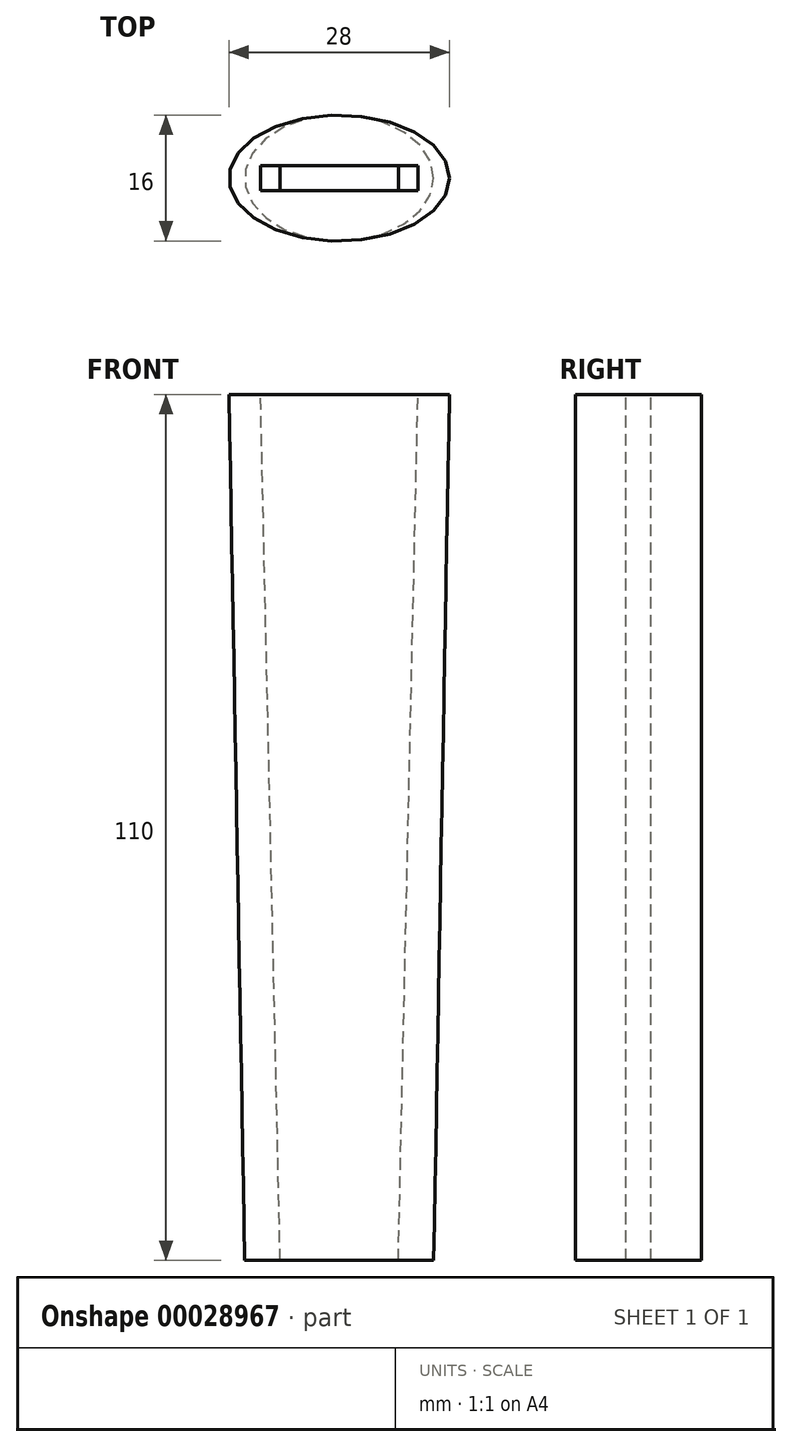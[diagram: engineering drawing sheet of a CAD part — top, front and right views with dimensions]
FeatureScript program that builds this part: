
annotation { "Feature Type Name" : "Feature", "Feature Type Description" : "" }
export const myFeature = defineFeature(function(context is Context, id is Id, definition is map)
    precondition{}
    {
        {
            var Q0;
            Q0=qCreatedBy(makeId("Top.planeOp"),FACE);
            var sketch = newSketch(context, id + "F0", { "sketchPlane" : qUnion([Q0])});
            skPoint(sketch, "E0", {"position": v(0, 0) * mm});
            skPoint(sketch, "E1", {"position": v(0, 8) * mm});
            skPoint(sketch, "E2", {"position": v(12, 0) * mm});
            skLineSegment(sketch, "E3", {"start": v(0, 0) * mm, "end": v(0, 8) * mm, "construction": true});
            skLineSegment(sketch, "E4", {"start": v(0, 0) * mm, "end": v(12, 0) * mm, "construction": true});
            skEllipse(sketch, "E5", {"center": v(0, 0) * mm, "majorRadius": 12 * mm, "minorRadius": 8 * mm, "majorAxis": v(1, 0)});
            skSolve(sketch);
        }
        {
            var Q0;
            Q0=makeQuery(id+"F0.imprint","IMPRINT",FACE,{"disambiguationData":[TD([[makeQuery(id+"F0.imprint","IMPRINT",EDGE,{"derivedFrom":sQuery(id+"F0.wireOp",EDGE,"E5")}),1.0]])]});
            cPlane(context, id + "F1", {"entities" : qUnion([Q0]), "cplaneType" : CPlaneType.OFFSET, "offset" : 110 * mm, "width" : 150 * mm, "height" : 150 * mm});
        }
        {
            var Q0;
            Q0=qCreatedBy(id+"F1.planeOp",FACE);
            var sketch = newSketch(context, id + "F2", { "sketchPlane" : qUnion([Q0])});
            skEllipse(sketch, "E6", {"center": v(0, 0) * mm, "majorRadius": 14 * mm, "minorRadius": 8 * mm, "majorAxis": v(-1, 0)});
            skSolve(sketch);
        }
        {
            var Q0;
            Q0=makeQuery(id+"F0.imprint","IMPRINT",FACE,{"disambiguationData":[TD([[makeQuery(id+"F0.imprint","IMPRINT",EDGE,{"derivedFrom":sQuery(id+"F0.wireOp",EDGE,"E5")}),1.0]])]});
            var Q1;
            Q1=makeQuery(id+"F2.imprint","IMPRINT",FACE,{"disambiguationData":[TD([[makeQuery(id+"F2.imprint","IMPRINT",EDGE,{"derivedFrom":sQuery(id+"F2.wireOp",EDGE,"E6")}),1.0]])]});
            loft(context, id + "F3", {"sheetProfilesArray" : [{ "sheetProfileEntities" : qUnion([Q0]) }, { "sheetProfileEntities" : qUnion([Q1]) }]});
        }
        {
            var Q0;
            Q0=makeQuery(id+"F3.opLoft","CAP_FACE",FACE,{"disambiguationData":[OSD([makeQuery(id+"F0.imprint","IMPRINT",FACE,{"disambiguationData":[TD([[makeQuery(id+"F0.imprint","IMPRINT",EDGE,{"derivedFrom":sQuery(id+"F0.wireOp",EDGE,"E5")}),1.0]])]})])],"isStart":true});
            var sketch = newSketch(context, id + "F4", { "sketchPlane" : qUnion([Q0])});
            skSolve(sketch);
        }
        {
            var Q0;
            Q0=makeQuery(id+"F4.imprint","IMPRINT",FACE,{"disambiguationData":[TD([[makeQuery(id+"F4.imprint","IMPRINT",EDGE,{"derivedFrom":makeQuery(id+"F3.opLoft","MID_CAP_EDGE",EDGE,{"disambiguationData":[OSD([sQuery(id+"F0.wireOp",EDGE,"E5")])],"capPos":0.0})}),1.0]])]});
            var sketch = newSketch(context, id + "F5", { "sketchPlane" : qUnion([Q0])});
            skLineSegment(sketch, "E7.rect.bottom", {"start": v(7.5, 1.6) * mm, "end": v(-7.5, 1.6) * mm});
            skLineSegment(sketch, "E7.rect.top", {"start": v(7.5, -1.6) * mm, "end": v(-7.5, -1.6) * mm});
            skLineSegment(sketch, "E7.rect.left", {"start": v(7.5, 1.6) * mm, "end": v(7.5, -1.6) * mm});
            skLineSegment(sketch, "E7.rect.right", {"start": v(-7.5, 1.6) * mm, "end": v(-7.5, -1.6) * mm});
            skPoint(sketch, "E7.rect.middle", {"position": v(0, 0) * mm});
            skSolve(sketch);
        }
        {
            var Q0;
            Q0=makeQuery(id+"F3.opLoft","CAP_FACE",FACE,{"disambiguationData":[OSD([makeQuery(id+"F2.imprint","IMPRINT",FACE,{"disambiguationData":[TD([[makeQuery(id+"F2.imprint","IMPRINT",EDGE,{"derivedFrom":sQuery(id+"F2.wireOp",EDGE,"E6")}),1.0]])]})])],"isStart":true});
            var sketch = newSketch(context, id + "F6", { "sketchPlane" : qUnion([Q0])});
            skPoint(sketch, "E8.0", {"position": v(0, 0) * mm});
            skLineSegment(sketch, "E9.rect.bottom", {"start": v(10, 1.6) * mm, "end": v(-10, 1.6) * mm});
            skLineSegment(sketch, "E9.rect.top", {"start": v(10, -1.6) * mm, "end": v(-10, -1.6) * mm});
            skLineSegment(sketch, "E9.rect.left", {"start": v(10, 1.6) * mm, "end": v(10, -1.6) * mm});
            skLineSegment(sketch, "E9.rect.right", {"start": v(-10, 1.6) * mm, "end": v(-10, -1.6) * mm});
            skSolve(sketch);
        }
        {
            var Q1;
            Q1=makeQuery(id+"F5.imprint","IMPRINT",FACE,{"disambiguationData":[TD([[makeQuery(id+"F5.imprint","IMPRINT",EDGE,{"derivedFrom":sQuery(id+"F5.wireOp",EDGE,"E7.rect.bottom")}),1.0]])]});
            var Q2;
            Q2=makeQuery(id+"F6.imprint","IMPRINT",FACE,{"disambiguationData":[TD([[makeQuery(id+"F6.imprint","IMPRINT",EDGE,{"derivedFrom":sQuery(id+"F6.wireOp",EDGE,"E9.rect.bottom")}),1.0]])]});
            loft(context, id + "F7", {"operationType" : NewBodyOperationType.REMOVE, "sheetProfilesArray" : [{ "sheetProfileEntities" : qUnion([Q1]) }, { "sheetProfileEntities" : qUnion([Q2]) }]});
        }
    });
